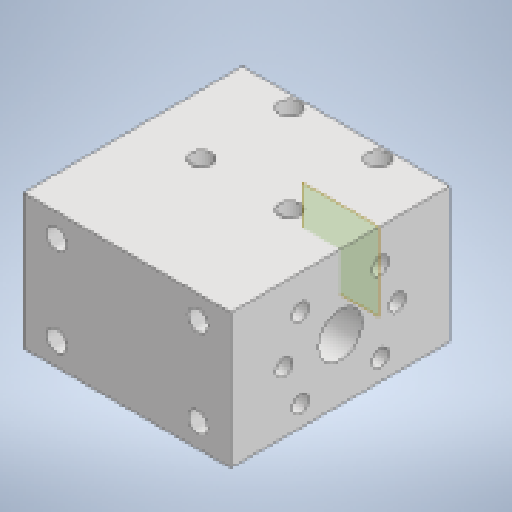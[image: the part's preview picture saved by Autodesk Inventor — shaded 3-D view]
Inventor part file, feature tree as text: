
AUTODESK INVENTOR PART (.ipt)
format: ipt  version: 2023 (Build 270158000, 158)  size: 259,584 bytes
history: native  units: mm
features: extrude x6, sketch x6, reference x4, other x3, plane x1, mirror x1
ambient origin geometry x8: Origin, YZ Plane, XZ Plane, XY Plane, X Axis, Y Axis, Z Axis, Center Point
bodies: Solid1 (feature_tree)
feature tree (21):
  extrude  "Extrusion1"  Depth=25.0mm
  extrude  "Extrusion2"  Depth=32.0mm
  extrude  "Extrusion3"  Depth=4.8mm
  extrude  "Extrusion4"  Depth=32.0mm
  extrude  "Extrusion5"  Depth=31.0mm
  extrude  "Extrusion6"  Depth=10.0mm TaperAngle=0.0deg
  plane  "Work Plane1"
  mirror  "Mirror1"
  sketch  "Sketch1"  dims[d0=3.0mm d1=25.0mm]
  sketch  "Sketch2"  dims[d2=32.0mm d3=58.8mm]
  sketch  "Sketch3"  dims[d4=2.0mm d5=0.0mm d6=4.8mm]
  sketch  "Sketch4"  dims[d7=32.0mm d9=15.2mm]
  reference  "Reference1"
  reference  "Reference2"
  reference  "Reference3"
  reference  "Reference4"
  sketch  "Sketch5"  dims[d11=45.0deg d12=31.0mm]
  sketch  "Sketch6"  dims[d14=21.0mm d15=2.0mm d16=0.0mm d17=12.5mm d18=20.05mm d19=27.05mm d20=0.0mm d21=6.0mm d22=2.0mm d23=0.0mm d24=5.7mm d25=40.0mm d26=25.0mm d27=15.0mm d28=0.0mm d29=31.0mm d30=31.0mm d31=10.0mm d32=0.0mm]
  other  "<userpath>\Desktop\CNC_Project\Frame_Gantry_Carrier.iam"
  other  "Frame_Gantry_Carrier.iam"
  other  "MGN15H-Carrier:1"
